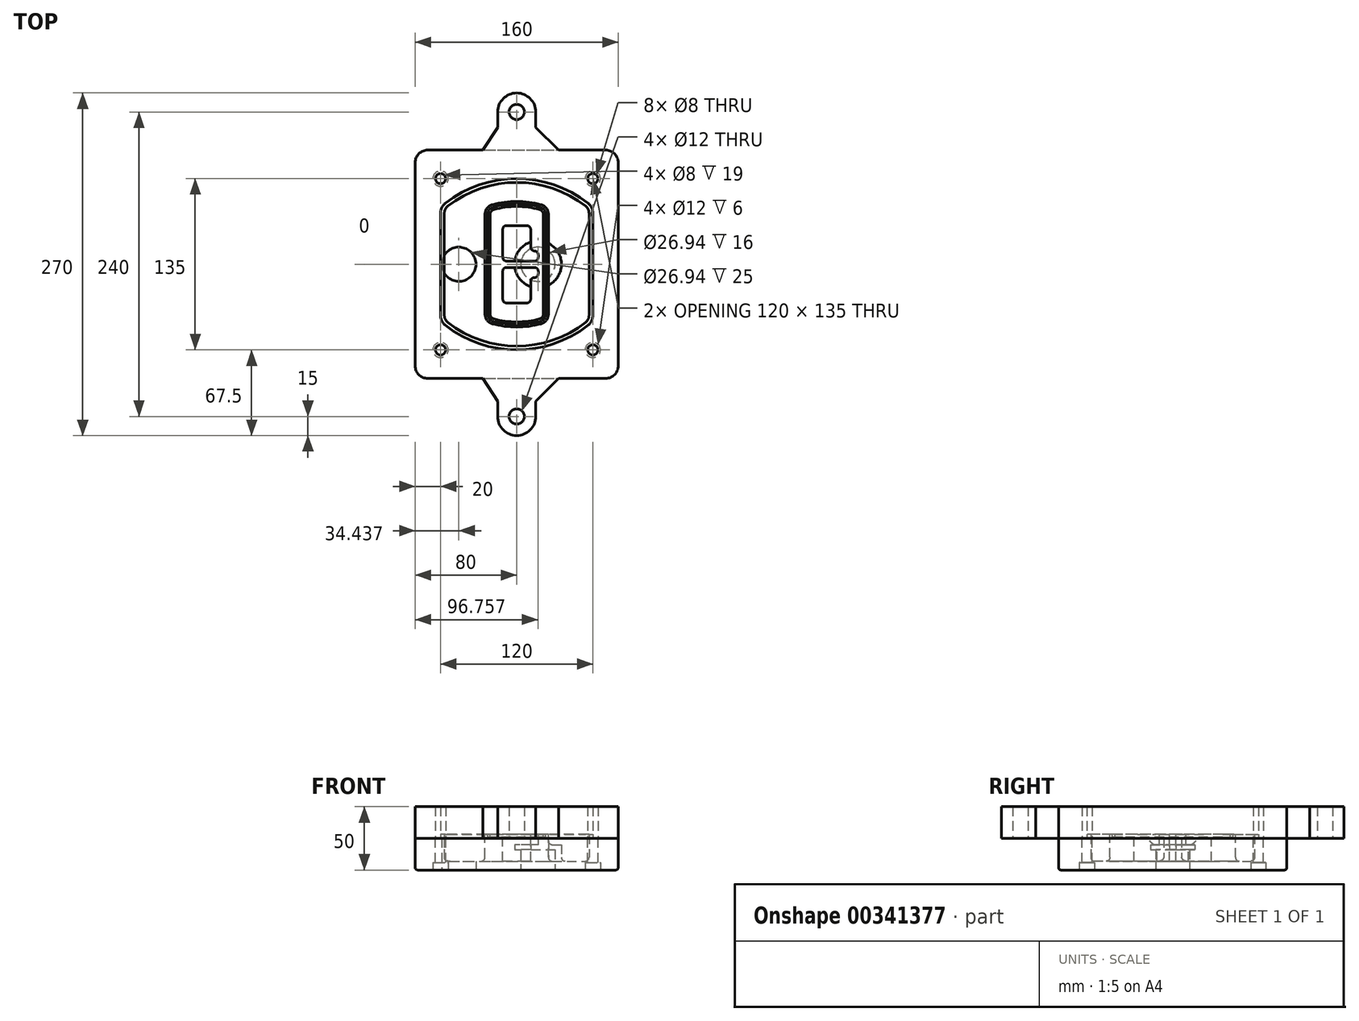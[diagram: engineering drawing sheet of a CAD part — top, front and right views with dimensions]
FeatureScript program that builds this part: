
annotation { "Feature Type Name" : "Feature", "Feature Type Description" : "" }
export const myFeature = defineFeature(function(context is Context, id is Id, definition is map)
    precondition{}
    {
        {
            var Q0;
            Q0=qCreatedBy(makeId("Top.planeOp"),FACE);
            var sketch = newSketch(context, id + "F0", { "sketchPlane" : qUnion([Q0])});
            skPoint(sketch, "E0.rect.middle", {"position": v(0, 0) * mm});
            skLineSegment(sketch, "E1.bottom", {"start": v(-70, -90) * mm, "end": v(70, -90) * mm});
            skLineSegment(sketch, "E1.top", {"start": v(-70, 90) * mm, "end": v(70, 90) * mm});
            skLineSegment(sketch, "E1.left", {"start": v(-80, -80) * mm, "end": v(-80, 80) * mm});
            skLineSegment(sketch, "E1.right", {"start": v(80, -80) * mm, "end": v(80, 80) * mm});
            skLineSegment(sketch, "E2", {"start": v(-80, 90) * mm, "end": v(80, -90) * mm, "construction": true});
            skLineSegment(sketch, "E3", {"start": v(80, 90) * mm, "end": v(-80, -90) * mm, "construction": true});
            skCircle(sketch, "E4", {"center": v(-60, 67.5) * mm, "radius": 4 * mm});
            skCircle(sketch, "E5", {"center": v(60, 67.5) * mm, "radius": 4 * mm});
            skCircle(sketch, "E6", {"center": v(60, -67.5) * mm, "radius": 4 * mm});
            skCircle(sketch, "E7", {"center": v(-60, -67.5) * mm, "radius": 4 * mm});
            skLineSegment(sketch, "E8", {"start": v(-60, 67.5) * mm, "end": v(60, 67.5) * mm, "construction": true});
            skLineSegment(sketch, "E9", {"start": v(60, 67.5) * mm, "end": v(60, -67.5) * mm, "construction": true});
            skLineSegment(sketch, "E10", {"start": v(60, -67.5) * mm, "end": v(-60, -67.5) * mm, "construction": true});
            skLineSegment(sketch, "E11", {"start": v(-60, -67.5) * mm, "end": v(-60, 67.5) * mm, "construction": true});
            skLineSegment(sketch, "E12", {"start": v(-60, 40.3) * mm, "end": v(-60, -40.3) * mm});
            skLineSegment(sketch, "E13", {"start": v(60, 40.3) * mm, "end": v(60, -40.3) * mm});
            skArc(sketch, "E14", {"start": v(56.15, 48.18) * mm, "mid": v(0, 67.5) * mm, "end": v(-56.15, 48.18) * mm});
            skArc(sketch, "E15", {"start": v(-56.15, -48.18) * mm, "mid": v(0, -67.5) * mm, "end": v(56.15, -48.18) * mm});
            skLineSegment(sketch, "E16", {"start": v(-60, 0) * mm, "end": v(60, 0) * mm, "construction": true});
            skPoint(sketch, "E17.visualSharp", {"position": v(-60, -45) * mm});
            skArc(sketch, "E17.filletArc", {"start": v(-60, -40.3) * mm, "mid": v(-58.99, -44.68) * mm, "end": v(-56.15, -48.18) * mm});
            skPoint(sketch, "E18.visualSharp", {"position": v(-60, 45) * mm});
            skArc(sketch, "E18.filletArc", {"start": v(-56.15, 48.18) * mm, "mid": v(-58.99, 44.68) * mm, "end": v(-60, 40.3) * mm});
            skPoint(sketch, "E19.visualSharp", {"position": v(60, 45) * mm});
            skArc(sketch, "E19.filletArc", {"start": v(60, 40.3) * mm, "mid": v(58.99, 44.68) * mm, "end": v(56.15, 48.18) * mm});
            skPoint(sketch, "E20.visualSharp", {"position": v(60, -45) * mm});
            skArc(sketch, "E20.filletArc", {"start": v(56.15, -48.18) * mm, "mid": v(58.99, -44.68) * mm, "end": v(60, -40.3) * mm});
            skPoint(sketch, "E21.visualSharp", {"position": v(-80, 90) * mm});
            skArc(sketch, "E21.filletArc", {"start": v(-70, 90) * mm, "mid": v(-77.07, 87.07) * mm, "end": v(-80, 80) * mm});
            skPoint(sketch, "E22.visualSharp", {"position": v(80, 90) * mm});
            skArc(sketch, "E22.filletArc", {"start": v(80, 80) * mm, "mid": v(77.07, 87.07) * mm, "end": v(70, 90) * mm});
            skPoint(sketch, "E23.visualSharp", {"position": v(80, -90) * mm});
            skArc(sketch, "E23.filletArc", {"start": v(70, -90) * mm, "mid": v(77.07, -87.07) * mm, "end": v(80, -80) * mm});
            skPoint(sketch, "E24.visualSharp", {"position": v(-80, -90) * mm});
            skArc(sketch, "E24.filletArc", {"start": v(-80, -80) * mm, "mid": v(-77.07, -87.07) * mm, "end": v(-70, -90) * mm});
            skArc(sketch, "E25.0", {"start": v(57, 40.3) * mm, "mid": v(56.3, 43.36) * mm, "end": v(54.3, 45.81) * mm});
            skLineSegment(sketch, "E25.1", {"start": v(57, 40.3) * mm, "end": v(57, -40.3) * mm});
            skArc(sketch, "E25.2", {"start": v(54.3, -45.81) * mm, "mid": v(56.3, -43.36) * mm, "end": v(57, -40.3) * mm});
            skArc(sketch, "E25.3", {"start": v(-54.3, -45.81) * mm, "mid": v(0, -64.5) * mm, "end": v(54.3, -45.81) * mm});
            skArc(sketch, "E25.4", {"start": v(-57, -40.3) * mm, "mid": v(-56.3, -43.36) * mm, "end": v(-54.3, -45.81) * mm});
            skArc(sketch, "E25.5", {"start": v(54.3, 45.81) * mm, "mid": v(0, 64.5) * mm, "end": v(-54.3, 45.81) * mm});
            skLineSegment(sketch, "E25.6", {"start": v(-57, 40.3) * mm, "end": v(-57, -40.3) * mm});
            skArc(sketch, "E25.7", {"start": v(-54.3, 45.81) * mm, "mid": v(-56.3, 43.36) * mm, "end": v(-57, 40.3) * mm});
            skArc(sketch, "E26.0", {"start": v(-58.62, 51.33) * mm, "mid": v(-62.58, 46.43) * mm, "end": v(-64, 40.3) * mm});
            skArc(sketch, "E26.1", {"start": v(58.62, 51.33) * mm, "mid": v(0, 71.5) * mm, "end": v(-58.62, 51.33) * mm});
            skArc(sketch, "E26.2", {"start": v(64, 40.3) * mm, "mid": v(62.58, 46.43) * mm, "end": v(58.62, 51.33) * mm});
            skLineSegment(sketch, "E26.3", {"start": v(64, 40.3) * mm, "end": v(64, -40.3) * mm});
            skArc(sketch, "E26.4", {"start": v(58.62, -51.33) * mm, "mid": v(62.58, -46.43) * mm, "end": v(64, -40.3) * mm});
            skLineSegment(sketch, "E26.5", {"start": v(-64, 40.3) * mm, "end": v(-64, -40.3) * mm});
            skArc(sketch, "E26.6", {"start": v(-58.62, -51.33) * mm, "mid": v(0, -71.5) * mm, "end": v(58.62, -51.33) * mm});
            skArc(sketch, "E26.7", {"start": v(-64, -40.3) * mm, "mid": v(-62.58, -46.43) * mm, "end": v(-58.62, -51.33) * mm});
            skSolve(sketch);
        }
        {
            var Q0;
            Q0=makeQuery(id+"F0.imprint","IMPRINT",FACE,{"disambiguationData":[TD([[makeQuery(id+"F0.imprint","IMPRINT",EDGE,{"derivedFrom":sQuery(id+"F0.wireOp",EDGE,"E1.bottom")}),1.0]])]});
            var Q1;
            Q1=makeQuery(id+"F0.imprint","IMPRINT",FACE,{"disambiguationData":[TD([[makeQuery(id+"F0.imprint","IMPRINT",EDGE,{"derivedFrom":sQuery(id+"F0.wireOp",EDGE,"E12")}),1.0]])]});
            var Q2;
            Q2=makeQuery(id+"F0.imprint","IMPRINT",FACE,{"disambiguationData":[TD([[makeQuery(id+"F0.imprint","IMPRINT",EDGE,{"derivedFrom":sQuery(id+"F0.wireOp",EDGE,"E25.0")}),1.0]])]});
            var Q3;
            Q3=makeQuery(id+"F0.imprint","IMPRINT",FACE,{"disambiguationData":[TD([[makeQuery(id+"F0.imprint","IMPRINT",EDGE,{"derivedFrom":sQuery(id+"F0.wireOp",EDGE,"E12")}),-1.0]])]});
            extrude(context, id + "F1", {"entities" : qUnion([Q0, Q1, Q2, Q3]), "oppositeDirection" : true, "depth" : 25 * mm});
        }
        {
            var Q0;
            Q0=makeQuery(id+"F0.imprint","IMPRINT",FACE,{"disambiguationData":[TD([[makeQuery(id+"F0.imprint","IMPRINT",EDGE,{"derivedFrom":sQuery(id+"F0.wireOp",EDGE,"E12")}),1.0]])]});
            extrude(context, id + "F2", {"entities" : qUnion([Q0]), "operationType" : NewBodyOperationType.ADD, "depth" : 3 * mm});
        }
        {
            var Q0;
            Q0=makeQuery(id+"F0.imprint","IMPRINT",FACE,{"disambiguationData":[TD([[makeQuery(id+"F0.imprint","IMPRINT",EDGE,{"derivedFrom":sQuery(id+"F0.wireOp",EDGE,"E25.0")}),1.0]])]});
            extrude(context, id + "F3", {"entities" : qUnion([Q0]), "operationType" : NewBodyOperationType.REMOVE, "oppositeDirection" : true, "depth" : 18 * mm});
        }
        {
            var Q0;
            Q0=makeQuery(id+"F2.opExtrude","CAP_FACE",FACE,{"disambiguationData":[OSD([sQuery(id+"F0.wireOp",EDGE,"E12"),sQuery(id+"F0.wireOp",EDGE,"E13"),sQuery(id+"F0.wireOp",EDGE,"E14"),sQuery(id+"F0.wireOp",EDGE,"E15"),sQuery(id+"F0.wireOp",EDGE,"E17.filletArc"),sQuery(id+"F0.wireOp",EDGE,"E18.filletArc"),sQuery(id+"F0.wireOp",EDGE,"E19.filletArc"),sQuery(id+"F0.wireOp",EDGE,"E20.filletArc"),sQuery(id+"F0.wireOp",EDGE,"E25.0"),sQuery(id+"F0.wireOp",EDGE,"E25.1"),sQuery(id+"F0.wireOp",EDGE,"E25.2"),sQuery(id+"F0.wireOp",EDGE,"E25.3"),sQuery(id+"F0.wireOp",EDGE,"E25.4"),sQuery(id+"F0.wireOp",EDGE,"E25.5"),sQuery(id+"F0.wireOp",EDGE,"E25.6"),sQuery(id+"F0.wireOp",EDGE,"E25.7")])],"isStart":false});
            var sketch = newSketch(context, id + "F4", { "sketchPlane" : qUnion([Q0])});
            skArc(sketch, "E27.0", {"start": v(-19.08, -46.97) * mm, "mid": v(0, -49.5) * mm, "end": v(19.08, -46.97) * mm});
            skArc(sketch, "E28.0", {"start": v(19.08, 46.97) * mm, "mid": v(0, 49.5) * mm, "end": v(-19.08, 46.97) * mm});
            skLineSegment(sketch, "E29", {"start": v(-25, 39.25) * mm, "end": v(-25, -39.25) * mm});
            skLineSegment(sketch, "E30", {"start": v(25, 39.25) * mm, "end": v(25, -39.25) * mm});
            skLineSegment(sketch, "E31", {"start": v(-25, 45.1) * mm, "end": v(25, 45.1) * mm, "construction": true});
            skLineSegment(sketch, "E32", {"start": v(-25, -45.1) * mm, "end": v(25, -45.1) * mm, "construction": true});
            skPoint(sketch, "E33.visualSharp", {"position": v(-25, 45.1) * mm});
            skArc(sketch, "E33.filletArc", {"start": v(-19.08, 46.97) * mm, "mid": v(-23.35, 44.11) * mm, "end": v(-25, 39.25) * mm});
            skPoint(sketch, "E34.visualSharp", {"position": v(25, 45.1) * mm});
            skArc(sketch, "E34.filletArc", {"start": v(25, 39.25) * mm, "mid": v(23.35, 44.11) * mm, "end": v(19.08, 46.97) * mm});
            skPoint(sketch, "E35.visualSharp", {"position": v(25, -45.1) * mm});
            skArc(sketch, "E35.filletArc", {"start": v(19.08, -46.97) * mm, "mid": v(23.35, -44.11) * mm, "end": v(25, -39.25) * mm});
            skPoint(sketch, "E36.visualSharp", {"position": v(-25, -45.1) * mm});
            skArc(sketch, "E36.filletArc", {"start": v(-25, -39.25) * mm, "mid": v(-23.35, -44.11) * mm, "end": v(-19.08, -46.97) * mm});
            skArc(sketch, "E37.0", {"start": v(54.3, 45.81) * mm, "mid": v(0, 64.5) * mm, "end": v(-54.3, 45.81) * mm});
            skArc(sketch, "E37.1", {"start": v(-54.3, 45.81) * mm, "mid": v(-56.3, 43.36) * mm, "end": v(-57, 40.3) * mm});
            skLineSegment(sketch, "E37.2", {"start": v(-57, 40.3) * mm, "end": v(-57, -40.3) * mm});
            skArc(sketch, "E37.3", {"start": v(-57, -40.3) * mm, "mid": v(-56.3, -43.36) * mm, "end": v(-54.3, -45.81) * mm});
            skArc(sketch, "E37.4", {"start": v(-54.3, -45.81) * mm, "mid": v(0, -64.5) * mm, "end": v(54.3, -45.81) * mm});
            skArc(sketch, "E37.5", {"start": v(54.3, -45.81) * mm, "mid": v(56.3, -43.36) * mm, "end": v(57, -40.3) * mm});
            skLineSegment(sketch, "E37.6", {"start": v(57, 40.3) * mm, "end": v(57, -40.3) * mm});
            skArc(sketch, "E37.7", {"start": v(57, 40.3) * mm, "mid": v(56.3, 43.36) * mm, "end": v(54.3, 45.81) * mm});
            skLineSegment(sketch, "E38.0", {"start": v(23, 39.25) * mm, "end": v(23, -39.25) * mm});
            skArc(sketch, "E38.1", {"start": v(18.56, -45.04) * mm, "mid": v(21.76, -42.9) * mm, "end": v(23, -39.25) * mm});
            skArc(sketch, "E38.2", {"start": v(-18.56, -45.04) * mm, "mid": v(0, -47.5) * mm, "end": v(18.56, -45.04) * mm});
            skArc(sketch, "E38.3", {"start": v(-23, -39.25) * mm, "mid": v(-21.76, -42.9) * mm, "end": v(-18.56, -45.04) * mm});
            skLineSegment(sketch, "E38.4", {"start": v(-23, 39.25) * mm, "end": v(-23, -39.25) * mm});
            skArc(sketch, "E38.5", {"start": v(23, 39.25) * mm, "mid": v(21.76, 42.9) * mm, "end": v(18.56, 45.04) * mm});
            skArc(sketch, "E38.6", {"start": v(-18.56, 45.04) * mm, "mid": v(-21.76, 42.9) * mm, "end": v(-23, 39.25) * mm});
            skArc(sketch, "E38.7", {"start": v(18.56, 45.04) * mm, "mid": v(0, 47.5) * mm, "end": v(-18.56, 45.04) * mm});
            skArc(sketch, "E39.0", {"start": v(21, 39.25) * mm, "mid": v(20.18, 41.68) * mm, "end": v(18.04, 43.1) * mm});
            skLineSegment(sketch, "E39.1", {"start": v(21, 39.25) * mm, "end": v(21, -39.25) * mm});
            skArc(sketch, "E39.2", {"start": v(18.04, -43.1) * mm, "mid": v(20.18, -41.68) * mm, "end": v(21, -39.25) * mm});
            skArc(sketch, "E39.3", {"start": v(-18.04, -43.1) * mm, "mid": v(0, -45.5) * mm, "end": v(18.04, -43.1) * mm});
            skArc(sketch, "E39.4", {"start": v(-21, -39.25) * mm, "mid": v(-20.18, -41.68) * mm, "end": v(-18.04, -43.1) * mm});
            skArc(sketch, "E39.5", {"start": v(18.04, 43.1) * mm, "mid": v(0, 45.5) * mm, "end": v(-18.04, 43.1) * mm});
            skLineSegment(sketch, "E39.6", {"start": v(-21, 39.25) * mm, "end": v(-21, -39.25) * mm});
            skArc(sketch, "E39.7", {"start": v(-18.04, 43.1) * mm, "mid": v(-20.18, 41.68) * mm, "end": v(-21, 39.25) * mm});
            skLineSegment(sketch, "E40", {"start": v(-25, 0) * mm, "end": v(25, 0) * mm, "construction": true});
            skLineSegment(sketch, "E41", {"start": v(-11, 5.5) * mm, "end": v(-11, 27.5) * mm});
            skLineSegment(sketch, "E42", {"start": v(-8, 30.5) * mm, "end": v(8, 30.5) * mm});
            skLineSegment(sketch, "E43", {"start": v(11, 27.5) * mm, "end": v(11, 13.5) * mm});
            skLineSegment(sketch, "E44", {"start": v(14, 10.5) * mm, "end": v(14, 10.5) * mm});
            skLineSegment(sketch, "E45", {"start": v(17, 7.5) * mm, "end": v(17, 5.5) * mm});
            skLineSegment(sketch, "E46", {"start": v(14, 2.5) * mm, "end": v(-8, 2.5) * mm});
            skPoint(sketch, "E47.visualSharp", {"position": v(-11, 30.5) * mm});
            skArc(sketch, "E47.filletArc", {"start": v(-8, 30.5) * mm, "mid": v(-10.12, 29.62) * mm, "end": v(-11, 27.5) * mm});
            skPoint(sketch, "E48.visualSharp", {"position": v(11, 30.5) * mm});
            skArc(sketch, "E48.filletArc", {"start": v(11, 27.5) * mm, "mid": v(10.12, 29.62) * mm, "end": v(8, 30.5) * mm});
            skPoint(sketch, "E49.visualSharp", {"position": v(11, 10.5) * mm});
            skArc(sketch, "E49.filletArc", {"start": v(11, 13.5) * mm, "mid": v(11.88, 11.38) * mm, "end": v(14, 10.5) * mm});
            skPoint(sketch, "E50.visualSharp", {"position": v(17, 10.5) * mm});
            skArc(sketch, "E50.filletArc", {"start": v(17, 7.5) * mm, "mid": v(16.12, 9.62) * mm, "end": v(14, 10.5) * mm});
            skPoint(sketch, "E51.visualSharp", {"position": v(17, 2.5) * mm});
            skArc(sketch, "E51.filletArc", {"start": v(14, 2.5) * mm, "mid": v(16.12, 3.38) * mm, "end": v(17, 5.5) * mm});
            skPoint(sketch, "E52.visualSharp", {"position": v(-11, 2.5) * mm});
            skArc(sketch, "E52.filletArc", {"start": v(-11, 5.5) * mm, "mid": v(-10.12, 3.38) * mm, "end": v(-8, 2.5) * mm});
            skLineSegment(sketch, "E53.0.MirrorCS", {"start": v(14, -2.5) * mm, "end": v(-8, -2.5) * mm});
            skArc(sketch, "E54.0.MirrorCS", {"start": v(-11, -5.5) * mm, "mid": v(-10.12, -3.38) * mm, "end": v(-8, -2.5) * mm});
            skLineSegment(sketch, "E55.0.MirrorCS", {"start": v(-11, -5.5) * mm, "end": v(-11, -27.5) * mm});
            skArc(sketch, "E56.0.MirrorCS", {"start": v(-8, -30.5) * mm, "mid": v(-10.12, -29.62) * mm, "end": v(-11, -27.5) * mm});
            skLineSegment(sketch, "E57.0.MirrorCS", {"start": v(-8, -30.5) * mm, "end": v(8, -30.5) * mm});
            skArc(sketch, "E58.0.MirrorCS", {"start": v(11, -27.5) * mm, "mid": v(10.12, -29.62) * mm, "end": v(8, -30.5) * mm});
            skLineSegment(sketch, "E59.0.MirrorCS", {"start": v(11, -27.5) * mm, "end": v(11, -13.5) * mm});
            skArc(sketch, "E60.0.MirrorCS", {"start": v(11, -13.5) * mm, "mid": v(11.88, -11.38) * mm, "end": v(14, -10.5) * mm});
            skArc(sketch, "E61.0.MirrorCS", {"start": v(17, -7.5) * mm, "mid": v(16.12, -9.62) * mm, "end": v(14, -10.5) * mm});
            skLineSegment(sketch, "E62.0.MirrorCS", {"start": v(17, -7.5) * mm, "end": v(17, -5.5) * mm});
            skArc(sketch, "E63.0.MirrorCS", {"start": v(14, -2.5) * mm, "mid": v(16.12, -3.38) * mm, "end": v(17, -5.5) * mm});
            skSolve(sketch);
        }
        {
            var Q0;
            Q0=makeQuery(id+"F4.imprint","IMPRINT",FACE,{"disambiguationData":[TD([[makeQuery(id+"F4.imprint","IMPRINT",EDGE,{"derivedFrom":sQuery(id+"F4.wireOp",EDGE,"E27.0")}),1.0]])]});
            var Q1;
            Q1=makeQuery(id+"F4.imprint","IMPRINT",FACE,{"disambiguationData":[TD([[makeQuery(id+"F4.imprint","IMPRINT",EDGE,{"derivedFrom":sQuery(id+"F4.wireOp",EDGE,"E38.0")}),-1.0]])]});
            var Q2;
            Q2=makeQuery(id+"F4.imprint","IMPRINT",FACE,{"disambiguationData":[TD([[makeQuery(id+"F4.imprint","IMPRINT",EDGE,{"derivedFrom":sQuery(id+"F4.wireOp",EDGE,"E39.0")}),1.0]])]});
            extrude(context, id + "F5", {"entities" : qUnion([Q0, Q1, Q2]), "operationType" : NewBodyOperationType.ADD, "endBound" : BoundingType.UP_TO_NEXT, "oppositeDirection" : true, "depth" : 25 * mm});
        }
        {
            var Q0;
            Q0=makeQuery(id+"F4.imprint","IMPRINT",FACE,{"disambiguationData":[TD([[makeQuery(id+"F4.imprint","IMPRINT",EDGE,{"derivedFrom":sQuery(id+"F4.wireOp",EDGE,"E38.0")}),-1.0]])]});
            extrude(context, id + "F6", {"entities" : qUnion([Q0]), "operationType" : NewBodyOperationType.REMOVE, "oppositeDirection" : true, "depth" : 2 * mm});
        }
        {
            var Q0;
            Q0=makeQuery(id+"F1.opExtrude","CAP_FACE",FACE,{"disambiguationData":[OSD([sQuery(id+"F0.wireOp",EDGE,"E1.bottom"),sQuery(id+"F0.wireOp",EDGE,"E1.top"),sQuery(id+"F0.wireOp",EDGE,"E1.left"),sQuery(id+"F0.wireOp",EDGE,"E1.right"),sQuery(id+"F0.wireOp",EDGE,"E4"),sQuery(id+"F0.wireOp",EDGE,"E5"),sQuery(id+"F0.wireOp",EDGE,"E6"),sQuery(id+"F0.wireOp",EDGE,"E7"),sQuery(id+"F0.wireOp",EDGE,"E21.filletArc"),sQuery(id+"F0.wireOp",EDGE,"E22.filletArc"),sQuery(id+"F0.wireOp",EDGE,"E23.filletArc"),sQuery(id+"F0.wireOp",EDGE,"E24.filletArc")])],"isStart":false});
            var sketch = newSketch(context, id + "F7", { "sketchPlane" : qUnion([Q0])});
            skCircle(sketch, "E64", {"center": v(16.76, 0) * mm, "radius": 13.47 * mm});
            skCircle(sketch, "E65", {"center": v(-45.56, 0) * mm, "radius": 13.47 * mm});
            skLineSegment(sketch, "E66", {"start": v(80, 0) * mm, "end": v(-80, 0) * mm});
            skCircle(sketch, "E67", {"center": v(16.76, 0) * mm, "radius": 18.47 * mm});
            skCircle(sketch, "E68", {"center": v(60, -67.5) * mm, "radius": 6 * mm});
            skCircle(sketch, "E69", {"center": v(-60, -67.5) * mm, "radius": 6 * mm});
            skCircle(sketch, "E70", {"center": v(-60, 67.5) * mm, "radius": 6 * mm});
            skCircle(sketch, "E71", {"center": v(60, 67.5) * mm, "radius": 6 * mm});
            skSolve(sketch);
        }
        {
            var Q0;
            {var subQ1=sQuery(id+"F7.wireOp",EDGE,"E66");var subQ4=sQuery(id+"F7.wireOp",EDGE,"E64");var subQ6=makeQuery(id+"F7.imprint","INTERSECT",VERTEX,{"disambiguationData":[OD(0.0)],"derivedFrom":[subQ4,subQ1]});Q0=makeQuery(id+"F7.imprint","IMPRINT",FACE,{"disambiguationData":[TD([[makeQuery(id+"F7.imprint","IMPRINT",EDGE,{"disambiguationData":[TD([[subQ6,-1.0]])],"derivedFrom":subQ4}),-1.0]])]});}
            var Q1;
            {var subQ0=sQuery(id+"F7.wireOp",EDGE,"E66");var subQ1=sQuery(id+"F7.wireOp",EDGE,"E64");var subQ3=makeQuery(id+"F7.imprint","INTERSECT",VERTEX,{"disambiguationData":[OD(0.0)],"derivedFrom":[subQ1,subQ0]});Q1=makeQuery(id+"F7.imprint","IMPRINT",FACE,{"disambiguationData":[TD([[makeQuery(id+"F7.imprint","IMPRINT",EDGE,{"disambiguationData":[TD([[subQ3,-1.0]])],"derivedFrom":subQ1}),1.0]])]});}
            var Q2;
            {var subQ0=sQuery(id+"F7.wireOp",EDGE,"E66");var subQ1=sQuery(id+"F7.wireOp",EDGE,"E64");var subQ3=makeQuery(id+"F7.imprint","INTERSECT",VERTEX,{"disambiguationData":[OD(0.0)],"derivedFrom":[subQ1,subQ0]});Q2=makeQuery(id+"F7.imprint","IMPRINT",FACE,{"disambiguationData":[TD([[makeQuery(id+"F7.imprint","IMPRINT",EDGE,{"disambiguationData":[TD([[subQ3,1.0]])],"derivedFrom":subQ1}),1.0]])]});}
            var Q3;
            {var subQ1=sQuery(id+"F7.wireOp",EDGE,"E66");var subQ4=sQuery(id+"F7.wireOp",EDGE,"E64");var subQ6=makeQuery(id+"F7.imprint","INTERSECT",VERTEX,{"disambiguationData":[OD(0.0)],"derivedFrom":[subQ4,subQ1]});Q3=makeQuery(id+"F7.imprint","IMPRINT",FACE,{"disambiguationData":[TD([[makeQuery(id+"F7.imprint","IMPRINT",EDGE,{"disambiguationData":[TD([[subQ6,1.0]])],"derivedFrom":subQ4}),-1.0]])]});}
            extrude(context, id + "F8", {"entities" : qUnion([Q0, Q1, Q2, Q3]), "operationType" : NewBodyOperationType.ADD, "oppositeDirection" : true, "depth" : 20 * mm});
        }
        {
            var Q0;
            {var subQ0=sQuery(id+"F7.wireOp",EDGE,"E66");var subQ1=sQuery(id+"F7.wireOp",EDGE,"E64");var subQ3=makeQuery(id+"F7.imprint","INTERSECT",VERTEX,{"disambiguationData":[OD(0.0)],"derivedFrom":[subQ1,subQ0]});Q0=makeQuery(id+"F7.imprint","IMPRINT",FACE,{"disambiguationData":[TD([[makeQuery(id+"F7.imprint","IMPRINT",EDGE,{"disambiguationData":[TD([[subQ3,-1.0]])],"derivedFrom":subQ1}),1.0]])]});}
            var Q1;
            {var subQ0=sQuery(id+"F7.wireOp",EDGE,"E66");var subQ1=sQuery(id+"F7.wireOp",EDGE,"E64");var subQ3=makeQuery(id+"F7.imprint","INTERSECT",VERTEX,{"disambiguationData":[OD(0.0)],"derivedFrom":[subQ1,subQ0]});Q1=makeQuery(id+"F7.imprint","IMPRINT",FACE,{"disambiguationData":[TD([[makeQuery(id+"F7.imprint","IMPRINT",EDGE,{"disambiguationData":[TD([[subQ3,1.0]])],"derivedFrom":subQ1}),1.0]])]});}
            extrude(context, id + "F9", {"entities" : qUnion([Q0, Q1]), "operationType" : NewBodyOperationType.REMOVE, "oppositeDirection" : true, "depth" : 16 * mm});
        }
        {
            var Q0;
            {var subQ0=sQuery(id+"F7.wireOp",EDGE,"E66");var subQ1=sQuery(id+"F7.wireOp",EDGE,"E65");var subQ3=makeQuery(id+"F7.imprint","INTERSECT",VERTEX,{"disambiguationData":[OD(0.0)],"derivedFrom":[subQ1,subQ0]});Q0=makeQuery(id+"F7.imprint","IMPRINT",FACE,{"disambiguationData":[TD([[makeQuery(id+"F7.imprint","IMPRINT",EDGE,{"disambiguationData":[TD([[subQ3,-1.0]])],"derivedFrom":subQ1}),1.0]])]});}
            var Q1;
            {var subQ0=sQuery(id+"F7.wireOp",EDGE,"E66");var subQ1=sQuery(id+"F7.wireOp",EDGE,"E65");var subQ3=makeQuery(id+"F7.imprint","INTERSECT",VERTEX,{"disambiguationData":[OD(0.0)],"derivedFrom":[subQ1,subQ0]});Q1=makeQuery(id+"F7.imprint","IMPRINT",FACE,{"disambiguationData":[TD([[makeQuery(id+"F7.imprint","IMPRINT",EDGE,{"disambiguationData":[TD([[subQ3,1.0]])],"derivedFrom":subQ1}),1.0]])]});}
            var Q2;
            Q2 = qSketchRegion(id + "F16", true);
            extrude(context, id + "F10", {"entities" : qUnion([Q0, Q1, Q2]), "operationType" : NewBodyOperationType.REMOVE, "oppositeDirection" : true, "depth" : 25 * mm});
        }
        {
            var Q0;
            Q0=makeQuery(id+"F7.imprint","IMPRINT",FACE,{"disambiguationData":[TD([[makeQuery(id+"F7.imprint","IMPRINT",EDGE,{"derivedFrom":sQuery(id+"F7.wireOp",EDGE,"E68")}),1.0]])]});
            var Q1;
            Q1=makeQuery(id+"F7.imprint","IMPRINT",FACE,{"disambiguationData":[TD([[makeQuery(id+"F7.imprint","IMPRINT",EDGE,{"derivedFrom":makeQuery(id+"F1.opExtrude","CAP_EDGE",EDGE,{"disambiguationData":[OSD([sQuery(id+"F0.wireOp",EDGE,"E5")])],"isStart":false})}),-1.0]])]});
            var Q2;
            Q2=makeQuery(id+"F7.imprint","IMPRINT",FACE,{"disambiguationData":[TD([[makeQuery(id+"F7.imprint","IMPRINT",EDGE,{"derivedFrom":sQuery(id+"F7.wireOp",EDGE,"E69")}),1.0]])]});
            var Q3;
            Q3=makeQuery(id+"F7.imprint","IMPRINT",FACE,{"disambiguationData":[TD([[makeQuery(id+"F7.imprint","IMPRINT",EDGE,{"derivedFrom":makeQuery(id+"F1.opExtrude","CAP_EDGE",EDGE,{"disambiguationData":[OSD([sQuery(id+"F0.wireOp",EDGE,"E4")])],"isStart":false})}),-1.0]])]});
            var Q4;
            Q4=makeQuery(id+"F7.imprint","IMPRINT",FACE,{"disambiguationData":[TD([[makeQuery(id+"F7.imprint","IMPRINT",EDGE,{"derivedFrom":sQuery(id+"F7.wireOp",EDGE,"E70")}),1.0]])]});
            var Q5;
            Q5=makeQuery(id+"F7.imprint","IMPRINT",FACE,{"disambiguationData":[TD([[makeQuery(id+"F7.imprint","IMPRINT",EDGE,{"derivedFrom":makeQuery(id+"F1.opExtrude","CAP_EDGE",EDGE,{"disambiguationData":[OSD([sQuery(id+"F0.wireOp",EDGE,"E7")])],"isStart":false})}),-1.0]])]});
            var Q6;
            Q6=makeQuery(id+"F7.imprint","IMPRINT",FACE,{"disambiguationData":[TD([[makeQuery(id+"F7.imprint","IMPRINT",EDGE,{"derivedFrom":sQuery(id+"F7.wireOp",EDGE,"E71")}),1.0]])]});
            var Q7;
            Q7=makeQuery(id+"F7.imprint","IMPRINT",FACE,{"disambiguationData":[TD([[makeQuery(id+"F7.imprint","IMPRINT",EDGE,{"derivedFrom":makeQuery(id+"F1.opExtrude","CAP_EDGE",EDGE,{"disambiguationData":[OSD([sQuery(id+"F0.wireOp",EDGE,"E6")])],"isStart":false})}),-1.0]])]});
            extrude(context, id + "F11", {"entities" : qUnion([Q0, Q1, Q2, Q3, Q4, Q5, Q6, Q7]), "operationType" : NewBodyOperationType.REMOVE, "oppositeDirection" : true, "depth" : 6 * mm});
        }
        {
            var Q0;
            Q0=makeQuery(id+"F9.boolean.opBoolean","COPY",FACE,{"derivedFrom":makeQuery(id+"F9.opExtrude","CAP_FACE",FACE,{"disambiguationData":[OSD([sQuery(id+"F7.wireOp",EDGE,"E64")])],"isStart":false})});
            var sketch = newSketch(context, id + "F12", { "sketchPlane" : qUnion([Q0])});
            skArc(sketch, "E72.0", {"start": v(11, 17.55) * mm, "mid": v(2.57, 11.82) * mm, "end": v(-1.54, 2.5) * mm});
            skArc(sketch, "E72.1", {"start": v(-1.54, -2.5) * mm, "mid": v(2.57, -11.82) * mm, "end": v(11, -17.55) * mm});
            skLineSegment(sketch, "E73", {"start": v(-1.54, -2.5) * mm, "end": v(14, -2.5) * mm});
            skLineSegment(sketch, "E74.0", {"start": v(14, 2.5) * mm, "end": v(-1.54, 2.5) * mm});
            skArc(sketch, "E74.1", {"start": v(14, 2.5) * mm, "mid": v(16.12, 3.38) * mm, "end": v(17, 5.5) * mm});
            skLineSegment(sketch, "E74.2", {"start": v(17, 7.5) * mm, "end": v(17, 5.5) * mm});
            skArc(sketch, "E74.3", {"start": v(17, 7.5) * mm, "mid": v(16.12, 9.62) * mm, "end": v(14, 10.5) * mm});
            skArc(sketch, "E74.4", {"start": v(11, 13.5) * mm, "mid": v(11.88, 11.38) * mm, "end": v(14, 10.5) * mm});
            skLineSegment(sketch, "E74.5", {"start": v(11, 17.55) * mm, "end": v(11, 13.5) * mm});
            skLineSegment(sketch, "E74.7", {"start": v(14, -2.5) * mm, "end": v(-1.54, -2.5) * mm});
            skArc(sketch, "E74.8", {"start": v(14, -2.5) * mm, "mid": v(16.12, -3.38) * mm, "end": v(17, -5.5) * mm});
            skLineSegment(sketch, "E74.9", {"start": v(17, -7.5) * mm, "end": v(17, -5.5) * mm});
            skArc(sketch, "E74.10", {"start": v(17, -7.5) * mm, "mid": v(16.12, -9.62) * mm, "end": v(14, -10.5) * mm});
            skArc(sketch, "E74.11", {"start": v(11, -13.5) * mm, "mid": v(11.88, -11.38) * mm, "end": v(14, -10.5) * mm});
            skLineSegment(sketch, "E74.12", {"start": v(11, -17.55) * mm, "end": v(11, -13.5) * mm});
            skPoint(sketch, "E75.orphan", {"position": v(11, -27.5) * mm});
            skPoint(sketch, "E76.orphan", {"position": v(-8, -2.5) * mm});
            skPoint(sketch, "E77.orphan", {"position": v(-8, 2.5) * mm});
            skPoint(sketch, "E78.orphan", {"position": v(11, 27.5) * mm});
            skSolve(sketch);
        }
        {
            var Q0;
            {var subQ7=sQuery(id+"F12.wireOp",EDGE,"E72.0");var subQ14=sQuery(id+"F12.wireOp",EDGE,"E72.1");var subQ16=sQuery(id+"F12.wireOp",EDGE,"E74.1");var subQ18=sQuery(id+"F12.wireOp",EDGE,"E74.8");Q0=qUnion([makeQuery(id+"F12.imprint","IMPRINT",FACE,{"disambiguationData":[TD([[makeQuery(id+"F12.imprint","IMPRINT",EDGE,{"derivedFrom":subQ7}),1.0]])]}),makeQuery(id+"F12.imprint","IMPRINT",FACE,{"disambiguationData":[TD([[makeQuery(id+"F12.imprint","IMPRINT",EDGE,{"derivedFrom":subQ14}),1.0]])]}),makeQuery(id+"F12.imprint","IMPRINT",FACE,{"disambiguationData":[TD([[makeQuery(id+"F12.imprint","IMPRINT",EDGE,{"derivedFrom":subQ16}),1.0]])]}),makeQuery(id+"F12.imprint","IMPRINT",FACE,{"disambiguationData":[TD([[makeQuery(id+"F12.imprint","IMPRINT",EDGE,{"derivedFrom":subQ18}),-1.0]])]})]);}
            var Q1;
            Q1=makeQuery(id+"F5.boolean.opBoolean","SPLIT",FACE,{"disambiguationData":[TD([makeQuery(id+"F5.opExtrude","SWEPT_FACE",FACE,{"disambiguationData":[OSD([sQuery(id+"F4.wireOp",EDGE,"E41")])]})])],"derivedFrom":makeQuery(id+"F3.boolean.opBoolean","COPY",FACE,{"derivedFrom":makeQuery(id+"F3.opExtrude","CAP_FACE",FACE,{"disambiguationData":[OSD([sQuery(id+"F0.wireOp",EDGE,"E25.0"),sQuery(id+"F0.wireOp",EDGE,"E25.1"),sQuery(id+"F0.wireOp",EDGE,"E25.2"),sQuery(id+"F0.wireOp",EDGE,"E25.3"),sQuery(id+"F0.wireOp",EDGE,"E25.4"),sQuery(id+"F0.wireOp",EDGE,"E25.5"),sQuery(id+"F0.wireOp",EDGE,"E25.6"),sQuery(id+"F0.wireOp",EDGE,"E25.7")])],"isStart":false})})});
            extrude(context, id + "F13", {"entities" : qUnion([Q0]), "operationType" : NewBodyOperationType.REMOVE, "endBound" : BoundingType.UP_TO_SURFACE, "endBoundEntityFace" : qUnion([Q1]), "depth" : 25 * mm});
        }
        {
            var Q0;
            Q0=makeQuery(id+"F3.boolean.opBoolean","COPY",EDGE,{"derivedFrom":makeQuery(id+"F3.opExtrude","CAP_EDGE",EDGE,{"disambiguationData":[OSD([sQuery(id+"F0.wireOp",EDGE,"E25.6")])],"isStart":false})});
            var Q1;
            Q1=makeQuery(id+"F8.boolean.opBoolean","INTERSECT",EDGE,{"derivedFrom":[makeQuery(id+"F5.opExtrude","SWEPT_FACE",FACE,{"disambiguationData":[OSD([sQuery(id+"F4.wireOp",EDGE,"E30")])]}),makeQuery(id+"F8.opExtrude","CAP_FACE",FACE,{"disambiguationData":[OSD([sQuery(id+"F7.wireOp",EDGE,"E67")])],"isStart":false})]});
            var Q2;
            Q2=makeQuery(id+"F8.boolean.opBoolean","INTERSECT",EDGE,{"disambiguationData":[OD(1.0)],"derivedFrom":[makeQuery(id+"F5.opExtrude","SWEPT_FACE",FACE,{"disambiguationData":[OSD([sQuery(id+"F4.wireOp",EDGE,"E30")])]}),makeQuery(id+"F8.opExtrude","SWEPT_FACE",FACE,{"disambiguationData":[OSD([sQuery(id+"F7.wireOp",EDGE,"E67")])]})]});
            var Q3;
            {var subQ0=sQuery(id+"F4.wireOp",EDGE,"E30");Q3=makeQuery(id+"F8.boolean.opBoolean","SPLIT",EDGE,{"disambiguationData":[TD([makeQuery(id+"F5.opExtrude","SWEPT_FACE",FACE,{"disambiguationData":[OSD([sQuery(id+"F4.wireOp",EDGE,"E35.filletArc")])]})])],"derivedFrom":makeQuery(id+"F5.opExtrude","CAP_EDGE",EDGE,{"disambiguationData":[OSD([subQ0])],"isStart":false})});}
            var Q4;
            {var subQ0=sQuery(id+"F0.wireOp",EDGE,"E25.7");var subQ1=sQuery(id+"F0.wireOp",EDGE,"E25.1");var subQ2=sQuery(id+"F0.wireOp",EDGE,"E25.6");var subQ3=sQuery(id+"F0.wireOp",EDGE,"E25.5");var subQ4=sQuery(id+"F0.wireOp",EDGE,"E25.4");var subQ5=sQuery(id+"F0.wireOp",EDGE,"E25.0");var subQ6=sQuery(id+"F0.wireOp",EDGE,"E25.2");var subQ7=sQuery(id+"F0.wireOp",EDGE,"E25.3");Q4=makeQuery(id+"F8.boolean.opBoolean","INTERSECT",EDGE,{"derivedFrom":[makeQuery(id+"F5.boolean.opBoolean","SPLIT",FACE,{"disambiguationData":[TD([makeQuery(id+"F2.opExtrude","SWEPT_FACE",FACE,{"disambiguationData":[OSD([subQ5])]})])],"derivedFrom":makeQuery(id+"F3.boolean.opBoolean","COPY",FACE,{"derivedFrom":makeQuery(id+"F3.opExtrude","CAP_FACE",FACE,{"disambiguationData":[OSD([subQ5,subQ1,subQ6,subQ7,subQ4,subQ3,subQ2,subQ0])],"isStart":false})})}),makeQuery(id+"F8.opExtrude","SWEPT_FACE",FACE,{"disambiguationData":[OSD([sQuery(id+"F7.wireOp",EDGE,"E67")])]})]});}
            var Q5;
            Q5=makeQuery(id+"F8.boolean.opBoolean","INTERSECT",EDGE,{"disambiguationData":[OD(0.0)],"derivedFrom":[makeQuery(id+"F5.opExtrude","SWEPT_FACE",FACE,{"disambiguationData":[OSD([sQuery(id+"F4.wireOp",EDGE,"E30")])]}),makeQuery(id+"F8.opExtrude","SWEPT_FACE",FACE,{"disambiguationData":[OSD([sQuery(id+"F7.wireOp",EDGE,"E67")])]})]});
            fillet(context, id + "F14", {"entities" : qUnion([Q0, Q1, Q2, Q3, Q4, Q5]), "radius" : 3 * mm, "tangentPropagation" : true, "allowEdgeOverflow" : false});
        }
        {
            var Q0;
            Q0=makeQuery(id+"F1.opExtrude","CAP_EDGE",EDGE,{"disambiguationData":[OSD([sQuery(id+"F0.wireOp",EDGE,"E1.bottom")])],"isStart":false});
            fillet(context, id + "F15", {"entities" : qUnion([Q0]), "radius" : 2 * mm, "tangentPropagation" : true, "allowEdgeOverflow" : false});
        }
        {
            var Q0;
            {var subQ0=sQuery(id+"F0.wireOp",EDGE,"E21.filletArc");var subQ1=sQuery(id+"F0.wireOp",EDGE,"E7");var subQ2=sQuery(id+"F0.wireOp",EDGE,"E6");var subQ3=sQuery(id+"F0.wireOp",EDGE,"E5");var subQ4=sQuery(id+"F0.wireOp",EDGE,"E4");var subQ5=sQuery(id+"F0.wireOp",EDGE,"E22.filletArc");var subQ6=sQuery(id+"F0.wireOp",EDGE,"E1.bottom");var subQ7=sQuery(id+"F0.wireOp",EDGE,"E1.right");var subQ8=sQuery(id+"F0.wireOp",EDGE,"E1.top");var subQ9=sQuery(id+"F0.wireOp",EDGE,"E1.left");var subQ10=sQuery(id+"F0.wireOp",EDGE,"E23.filletArc");var subQ11=sQuery(id+"F0.wireOp",EDGE,"E24.filletArc");Q0=makeQuery(id+"F2.boolean.opBoolean","SPLIT",FACE,{"disambiguationData":[TD([makeQuery(id+"F1.opExtrude","SWEPT_FACE",FACE,{"disambiguationData":[OSD([subQ6])]})])],"derivedFrom":makeQuery(id+"F1.opExtrude","CAP_FACE",FACE,{"disambiguationData":[OSD([subQ6,subQ8,subQ9,subQ7,subQ4,subQ3,subQ2,subQ1,subQ0,subQ5,subQ10,subQ11])],"isStart":true})});}
            var sketch = newSketch(context, id + "F16", { "sketchPlane" : qUnion([Q0])});
            skLineSegment(sketch, "E79.0", {"start": v(-70, 90) * mm, "end": v(70, 90) * mm});
            skLineSegment(sketch, "E79.1", {"start": v(80, -80) * mm, "end": v(80, 80) * mm});
            skLineSegment(sketch, "E79.2", {"start": v(-70, -90) * mm, "end": v(70, -90) * mm});
            skLineSegment(sketch, "E79.3", {"start": v(-80, -80) * mm, "end": v(-80, 80) * mm});
            skArc(sketch, "E79.4", {"start": v(-70, 90) * mm, "mid": v(-77.07, 87.07) * mm, "end": v(-80, 80) * mm});
            skArc(sketch, "E79.5", {"start": v(80, 80) * mm, "mid": v(77.07, 87.07) * mm, "end": v(70, 90) * mm});
            skArc(sketch, "E79.6", {"start": v(70, -90) * mm, "mid": v(77.07, -87.07) * mm, "end": v(80, -80) * mm});
            skArc(sketch, "E79.7", {"start": v(-80, -80) * mm, "mid": v(-77.07, -87.07) * mm, "end": v(-70, -90) * mm});
            skArc(sketch, "E79.8", {"start": v(56.15, 48.18) * mm, "mid": v(0, 67.5) * mm, "end": v(-56.15, 48.18) * mm});
            skLineSegment(sketch, "E79.9", {"start": v(-60, 40.3) * mm, "end": v(-60, -40.3) * mm});
            skArc(sketch, "E79.10", {"start": v(-56.15, -48.18) * mm, "mid": v(0, -67.5) * mm, "end": v(56.15, -48.18) * mm});
            skLineSegment(sketch, "E79.11", {"start": v(60, 40.3) * mm, "end": v(60, -40.3) * mm});
            skArc(sketch, "E79.12", {"start": v(-56.15, 48.18) * mm, "mid": v(-58.99, 44.68) * mm, "end": v(-60, 40.3) * mm});
            skArc(sketch, "E79.13", {"start": v(60, 40.3) * mm, "mid": v(58.99, 44.68) * mm, "end": v(56.15, 48.18) * mm});
            skArc(sketch, "E79.14", {"start": v(56.15, -48.18) * mm, "mid": v(58.99, -44.68) * mm, "end": v(60, -40.3) * mm});
            skArc(sketch, "E79.15", {"start": v(-60, -40.3) * mm, "mid": v(-58.99, -44.68) * mm, "end": v(-56.15, -48.18) * mm});
            skCircle(sketch, "E79.16", {"center": v(-60, -67.5) * mm, "radius": 4 * mm});
            skCircle(sketch, "E79.17", {"center": v(60, -67.5) * mm, "radius": 4 * mm});
            skCircle(sketch, "E79.18", {"center": v(60, 67.5) * mm, "radius": 4 * mm});
            skCircle(sketch, "E79.19", {"center": v(-60, 67.5) * mm, "radius": 4 * mm});
            skLineSegment(sketch, "E80", {"start": v(-26.75, 90) * mm, "end": v(-15, 108) * mm});
            skLineSegment(sketch, "E81", {"start": v(-15, 108) * mm, "end": v(-15, 120) * mm});
            skCircle(sketch, "E82", {"center": v(0, 120) * mm, "radius": 6 * mm});
            skLineSegment(sketch, "E83", {"start": v(0, 120) * mm, "end": v(0, 90) * mm, "construction": true});
            skArc(sketch, "E84", {"start": v(-15, 120) * mm, "mid": v(0, 135) * mm, "end": v(15, 120) * mm});
            skLineSegment(sketch, "E85", {"start": v(15, 120) * mm, "end": v(15, 108) * mm});
            skLineSegment(sketch, "E86", {"start": v(15, 108) * mm, "end": v(33, 90) * mm});
            skLineSegment(sketch, "E87", {"start": v(-80, 0) * mm, "end": v(80, 0) * mm, "construction": true});
            skLineSegment(sketch, "E88.MirrorCS", {"start": v(-15, -108) * mm, "end": v(-15, -120) * mm});
            skLineSegment(sketch, "E89.MirrorCS", {"start": v(15, -120) * mm, "end": v(15, -108) * mm});
            skLineSegment(sketch, "E90.MirrorCS", {"start": v(15, -108) * mm, "end": v(33, -90) * mm});
            skCircle(sketch, "E91.MirrorC", {"center": v(0, -120) * mm, "radius": 6 * mm});
            skLineSegment(sketch, "E92.MirrorCS", {"start": v(-26.75, -90) * mm, "end": v(-15, -108) * mm});
            skArc(sketch, "E93.MirrorCS", {"start": v(-15, -120) * mm, "mid": v(0, -135) * mm, "end": v(15, -120) * mm});
            skLineSegment(sketch, "E94.MirrorCS", {"start": v(0, -120) * mm, "end": v(0, -90) * mm, "construction": true});
            skSolve(sketch);
        }
        {
            var Q0;
            Q0 = qSketchRegion(id + "F16", true);
            extrude(context, id + "F17", {"entities" : qUnion([Q0]), "depth" : 25 * mm});
        }
        {
            var Q0;
            Q0 = qSketchRegion(id + "F16", true);
            extrude(context, id + "F18", {"entities" : qUnion([Q0]), "depth" : 25 * mm});
        }
    });
